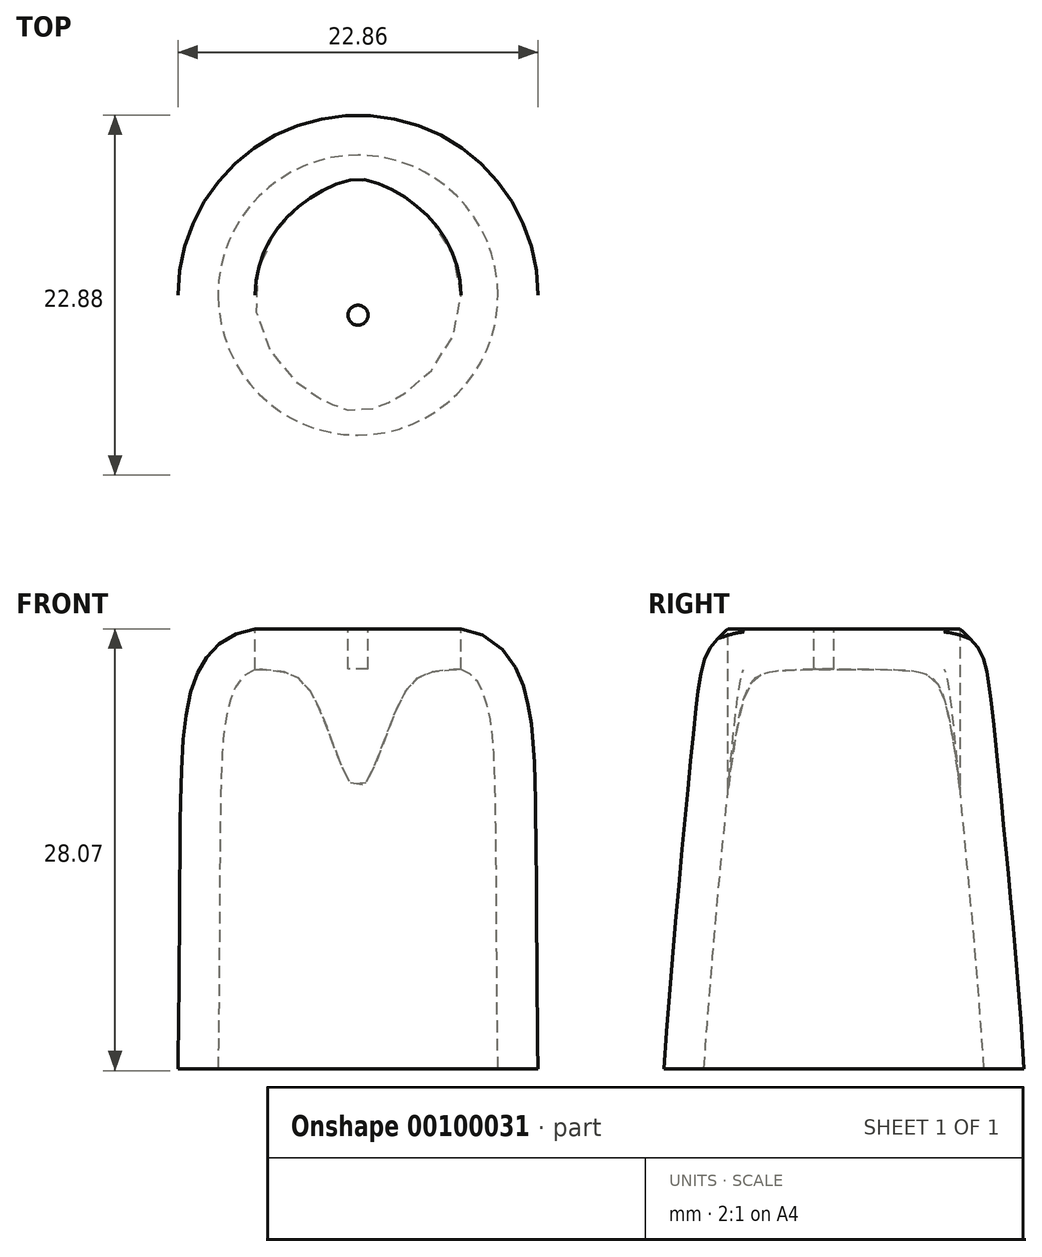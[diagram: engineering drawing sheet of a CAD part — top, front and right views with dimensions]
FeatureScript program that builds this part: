
annotation { "Feature Type Name" : "Feature", "Feature Type Description" : "" }
export const myFeature = defineFeature(function(context is Context, id is Id, definition is map)
    precondition{}
    {
        {
            var Q0;
            Q0=qCreatedBy(makeId("Top.planeOp"),FACE);
            var sketch = newSketch(context, id + "F0", { "sketchPlane" : qUnion([Q0])});
            skCircle(sketch, "E0", {"center": v(0, 0) * mm, "radius": 8.89 * mm});
            skSolve(sketch);
        }
        {
            var Q0;
            Q0=qCreatedBy(makeId("Top.planeOp"),FACE);
            cPlane(context, id + "F1", {"entities" : qUnion([Q0]), "cplaneType" : CPlaneType.OFFSET, "offset" : 25.4 * mm, "width" : 152.4 * mm, "height" : 152.4 * mm});
        }
        {
            var Q0;
            Q0=qCreatedBy(id+"F1.planeOp",FACE);
            var sketch = newSketch(context, id + "F2", { "sketchPlane" : qUnion([Q0])});
            skCircle(sketch, "E1", {"center": v(0, 0) * mm, "radius": 6.35 * mm});
            skSolve(sketch);
        }
        {
            var Q0;
            Q0=qCreatedBy(makeId("Front.planeOp"),FACE);
            var sketch = newSketch(context, id + "F3", { "sketchPlane" : qUnion([Q0])});
            skLineSegment(sketch, "E2", {"start": v(0, 0) * mm, "end": v(8.9, 0) * mm});
            skLineSegment(sketch, "E3", {"start": v(-0.1, 25.4) * mm, "end": v(6.35, 25.4) * mm});
            skPoint(sketch, "E4", {"position": v(-0.1, 25.4) * mm});
            skPoint(sketch, "E5", {"position": v(0, 0) * mm});
            skFitSpline(sketch, "E6", {"points": [v(8.9, 0) * mm, v(8.71, 17.58) * mm, v(6.35, 25.4) * mm], "startDerivative": vector(-0.6, 37.86) * mm, "endDerivative": vector(-15.7, 2.42) * mm});
            skLineSegment(sketch, "E7", {"start": v(0, 30.85) * mm, "end": v(0, -18.77) * mm, "construction": true});
            skLineSegment(sketch, "E8", {"start": v(-0.1, 25.4) * mm, "end": v(0, 0) * mm});
            skFitSpline(sketch, "E9.MirrorCS", {"points": [v(-8.89, 0) * mm, v(-8.71, 17.58) * mm, v(-6.35, 25.4) * mm], "startDerivative": vector(0.6, 37.86) * mm, "endDerivative": vector(15.7, 2.42) * mm});
            skSolve(sketch);
        }
        {
            var Q0;
            Q0=makeQuery(id+"F0.imprint","IMPRINT",FACE,{"disambiguationData":[TD([[makeQuery(id+"F0.imprint","IMPRINT",EDGE,{"derivedFrom":sQuery(id+"F0.wireOp",EDGE,"E0")}),1.0]])]});
            var Q1;
            Q1=makeQuery(id+"F2.imprint","IMPRINT",FACE,{"disambiguationData":[TD([[makeQuery(id+"F2.imprint","IMPRINT",EDGE,{"derivedFrom":sQuery(id+"F2.wireOp",EDGE,"E1")}),1.0]])]});
            var Q2;
            Q2=sQuery(id+"F3.wireOp",EDGE,"E6");
            var Q3;
            Q3=sQuery(id+"F3.wireOp",EDGE,"E9.MirrorCS");
            loft(context, id + "F4", {"addGuides" : true, "sheetProfilesArray" : [{ "sheetProfileEntities" : qUnion([Q0]) }, { "sheetProfileEntities" : qUnion([Q1]) }], "guidesArray" : [{ "guideEntities" : qUnion([Q2]), "guideDerivativeType" : LoftGuideDerivativeType.DEFAULT, "guideDerivativeMagnitude" : 1 }, { "guideEntities" : qUnion([Q3]), "guideDerivativeType" : LoftGuideDerivativeType.DEFAULT, "guideDerivativeMagnitude" : 1 }]});
        }
        {
            var Q0;
            Q0=makeQuery(id+"F4.opLoft","CAP_FACE",FACE,{"disambiguationData":[OSD([makeQuery(id+"F0.imprint","IMPRINT",FACE,{"disambiguationData":[TD([[makeQuery(id+"F0.imprint","IMPRINT",EDGE,{"derivedFrom":sQuery(id+"F0.wireOp",EDGE,"E0")}),1.0]])]})])],"isStart":true});
            shell(context, id + "F5", {"entities" : qUnion([Q0]), "thickness" : 2.54 * mm, "oppositeDirection" : true});
        }
        {
            var Q0;
            Q0=makeQuery(id+"F4.opLoft","CAP_FACE",FACE,{"disambiguationData":[OSD([makeQuery(id+"F2.imprint","IMPRINT",FACE,{"disambiguationData":[TD([[makeQuery(id+"F2.imprint","IMPRINT",EDGE,{"derivedFrom":sQuery(id+"F2.wireOp",EDGE,"E1")}),1.0]])]})])],"isStart":true});
            var sketch = newSketch(context, id + "F6", { "sketchPlane" : qUnion([Q0])});
            skCircle(sketch, "E10", {"center": v(0, 1.27) * mm, "radius": 0.64 * mm});
            skCircle(sketch, "E11.MirrorC", {"center": v(0, -1.27) * mm, "radius": 0.64 * mm});
            skSolve(sketch);
        }
        {
            var Q0;
            Q0=makeQuery(id+"F6.imprint","IMPRINT",FACE,{"disambiguationData":[TD([[makeQuery(id+"F6.imprint","IMPRINT",EDGE,{"derivedFrom":sQuery(id+"F6.wireOp",EDGE,"E10")}),1.0]])]});
            var Q1;
            Q1=makeQuery(id+"F6.imprint","IMPRINT",FACE,{"disambiguationData":[TD([[makeQuery(id+"F6.imprint","IMPRINT",EDGE,{"derivedFrom":sQuery(id+"F6.wireOp",EDGE,"E11.MirrorC")}),-1.0]])]});
            extrude(context, id + "F7", {"entities" : qUnion([Q0, Q1]), "operationType" : NewBodyOperationType.REMOVE, "endBound" : BoundingType.THROUGH_ALL, "oppositeDirection" : true, "depth" : 25.4 * mm});
        }
    });
